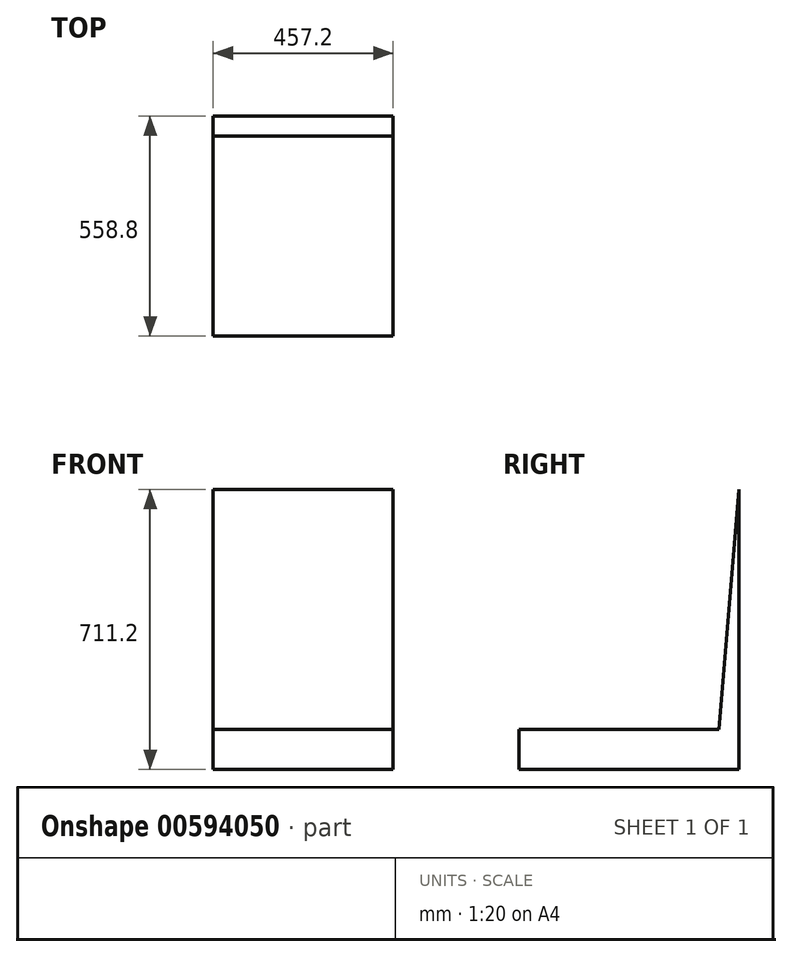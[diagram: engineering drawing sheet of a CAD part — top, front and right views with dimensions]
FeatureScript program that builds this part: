
annotation { "Feature Type Name" : "Feature", "Feature Type Description" : "" }
export const myFeature = defineFeature(function(context is Context, id is Id, definition is map)
    precondition{}
    {
        {
            var Q0;
            Q0=qCreatedBy(makeId("Right.planeOp"),FACE);
            var sketch = newSketch(context, id + "F0", { "sketchPlane" : qUnion([Q0])});
            skLineSegment(sketch, "E0", {"start": v(-93.87, -101.6) * mm, "end": v(-652.67, -101.6) * mm});
            skLineSegment(sketch, "E1", {"start": v(-93.87, -101.6) * mm, "end": v(-93.87, 609.6) * mm});
            skLineSegment(sketch, "E2", {"start": v(-652.67, -101.6) * mm, "end": v(-652.67, 0) * mm});
            skLineSegment(sketch, "E3", {"start": v(-652.67, 0) * mm, "end": v(-144.67, 0) * mm});
            skLineSegment(sketch, "E4", {"start": v(-93.87, 609.6) * mm, "end": v(-144.67, 0) * mm});
            skSolve(sketch);
        }
        {
            var Q0;
            Q0 = qSketchRegion(id + "F0", true);
            extrude(context, id + "F1", {"entities" : qUnion([Q0]), "depth" : 457.2 * mm, "offsetDistance" : 25.4 * mm});
        }
    });
